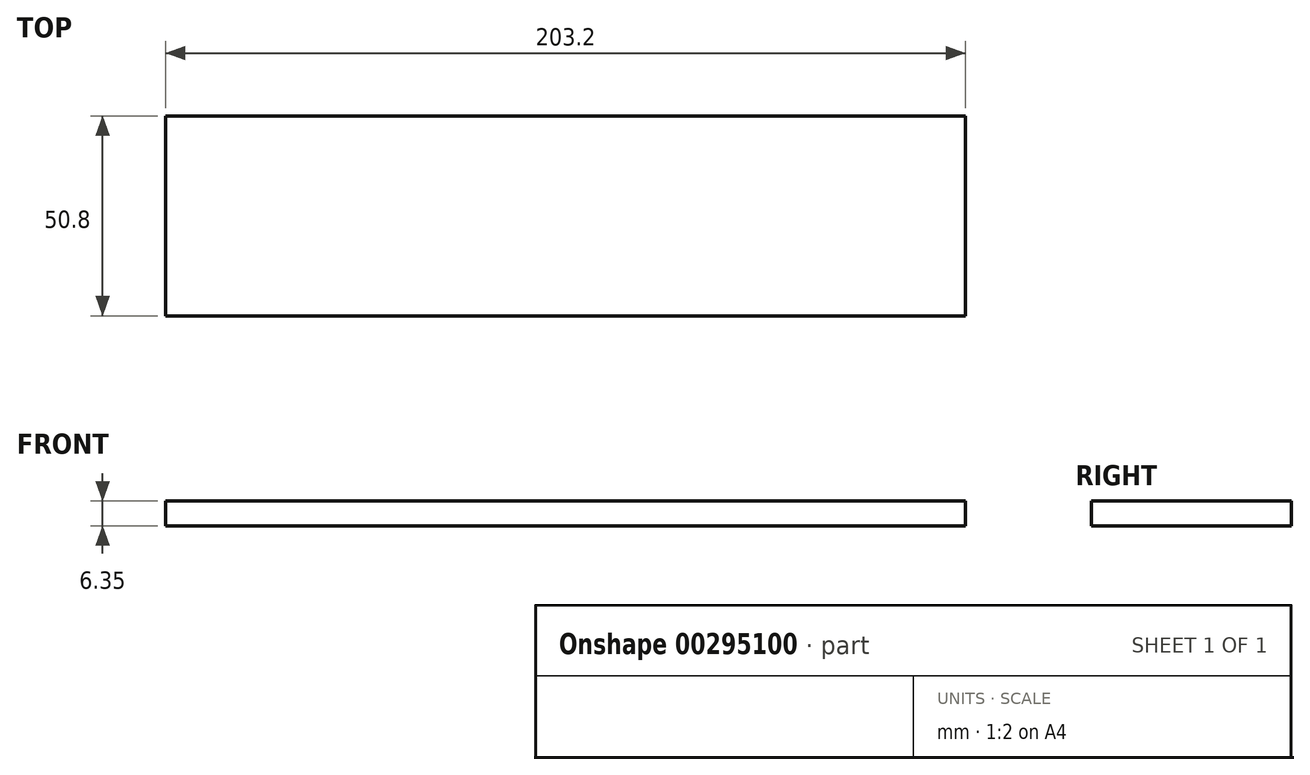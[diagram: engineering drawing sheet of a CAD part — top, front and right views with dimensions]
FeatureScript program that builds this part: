
annotation { "Feature Type Name" : "Feature", "Feature Type Description" : "" }
export const myFeature = defineFeature(function(context is Context, id is Id, definition is map)
    precondition{}
    {
        {
            var Q0;
            Q0=qCreatedBy(makeId("Top.planeOp"),FACE);
            var sketch = newSketch(context, id + "F0", { "sketchPlane" : qUnion([Q0])});
            skLineSegment(sketch, "E0.bottom", {"start": v(-70.16, 50.8) * mm, "end": v(133.04, 50.8) * mm});
            skLineSegment(sketch, "E0.top", {"start": v(-70.16, 0) * mm, "end": v(133.04, 0) * mm});
            skLineSegment(sketch, "E0.left", {"start": v(-70.16, 50.8) * mm, "end": v(-70.16, 0) * mm});
            skLineSegment(sketch, "E0.right", {"start": v(133.04, 50.8) * mm, "end": v(133.04, 0) * mm});
            skSolve(sketch);
        }
        {
            var Q0;
            Q0=makeQuery(id+"F0.imprint","IMPRINT",FACE,{"disambiguationData":[TD([[makeQuery(id+"F0.imprint","IMPRINT",EDGE,{"derivedFrom":sQuery(id+"F0.wireOp",EDGE,"E0.bottom")}),-1.0]])]});
            extrude(context, id + "F1", {"entities" : qUnion([Q0]), "depth" : 6.35 * mm});
        }
    });
